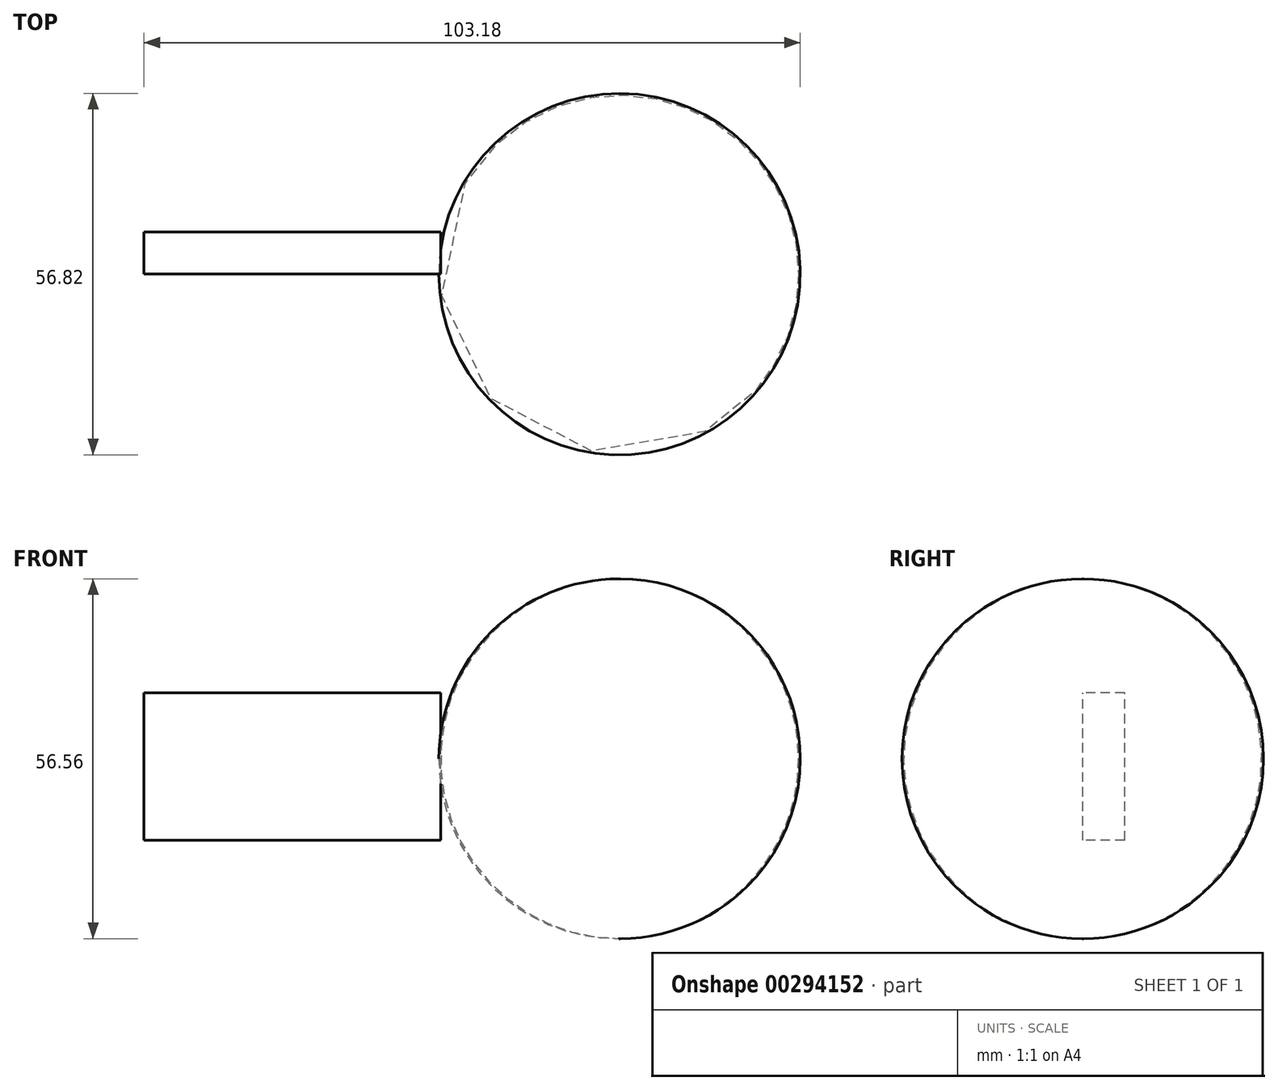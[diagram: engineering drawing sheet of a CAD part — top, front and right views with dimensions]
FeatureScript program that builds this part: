
annotation { "Feature Type Name" : "Feature", "Feature Type Description" : "" }
export const myFeature = defineFeature(function(context is Context, id is Id, definition is map)
    precondition{}
    {
        {
            var Q0;
            Q0=qCreatedBy(makeId("Right.planeOp"),FACE);
            var sketch = newSketch(context, id + "F0", { "sketchPlane" : qUnion([Q0])});
            skLineSegment(sketch, "E0", {"start": v(0, 0) * mm, "end": v(0, 56.56) * mm});
            skArc(sketch, "E1", {"start": v(0, 0) * mm, "mid": v(28.41, 28.28) * mm, "end": v(0, 56.56) * mm});
            skSolve(sketch);
        }
        {
            var Q0;
            Q0=makeQuery(id+"F0.imprint","IMPRINT",FACE,{"disambiguationData":[TD([[makeQuery(id+"F0.imprint","IMPRINT",EDGE,{"derivedFrom":sQuery(id+"F0.wireOp",EDGE,"E0")}),-1.0]])]});
            var Q1;
            Q1=sQuery(id+"F0.wireOp",EDGE,"E0");
            revolve(context, id + "F1", {"entities" : qUnion([Q0]), "axis" : qUnion([Q1]), "revolveType" : RevolveType.FULL});
        }
        {
            var Q0;
            Q0=qCreatedBy(makeId("Front.planeOp"),FACE);
            var sketch = newSketch(context, id + "F2", { "sketchPlane" : qUnion([Q0])});
            skLineSegment(sketch, "E2", {"start": v(-28.14, 27.04) * mm, "end": v(-74.77, 27.04) * mm});
            skLineSegment(sketch, "E3.bottom", {"start": v(-28.14, 15.45) * mm, "end": v(-74.77, 15.45) * mm});
            skLineSegment(sketch, "E3.top", {"start": v(-28.14, 38.63) * mm, "end": v(-74.77, 38.63) * mm});
            skLineSegment(sketch, "E3.left", {"start": v(-28.14, 15.45) * mm, "end": v(-28.14, 38.63) * mm});
            skLineSegment(sketch, "E3.right", {"start": v(-74.77, 15.45) * mm, "end": v(-74.77, 38.63) * mm});
            skPoint(sketch, "E3.middle", {"position": v(-51.45, 27.04) * mm});
            skSolve(sketch);
        }
        {
            var Q0;
            {var subQ0=sQuery(id+"F2.wireOp",EDGE,"E2");Q0=makeQuery(id+"F2.imprint","IMPRINT",FACE,{"disambiguationData":[TD([[makeQuery(id+"F2.imprint","IMPRINT",EDGE,{"derivedFrom":subQ0}),1.0]])]});}
            var Q1;
            {var subQ0=sQuery(id+"F2.wireOp",EDGE,"E2");Q1=makeQuery(id+"F2.imprint","IMPRINT",FACE,{"disambiguationData":[TD([[makeQuery(id+"F2.imprint","IMPRINT",EDGE,{"derivedFrom":subQ0}),-1.0]])]});}
            extrude(context, id + "F3", {"entities" : qUnion([Q0, Q1]), "oppositeDirection" : true, "depth" : 6.6 * mm});
        }
    });
